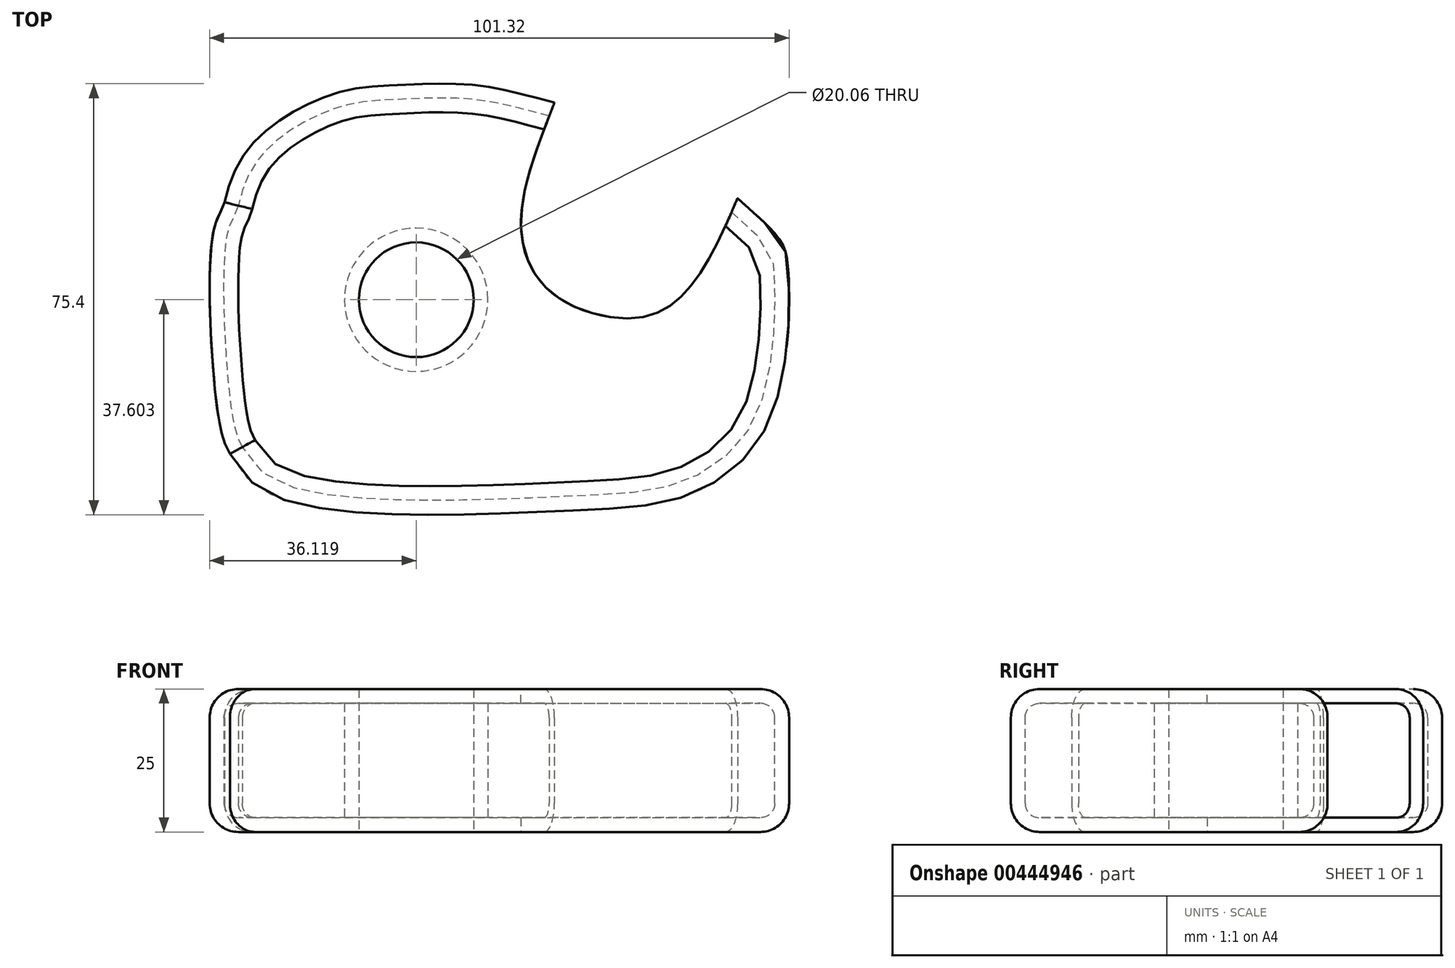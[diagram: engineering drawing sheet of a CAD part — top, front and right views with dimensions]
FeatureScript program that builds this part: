
annotation { "Feature Type Name" : "Feature", "Feature Type Description" : "" }
export const myFeature = defineFeature(function(context is Context, id is Id, definition is map)
    precondition{}
    {
        {
            var Q0;
            Q0=qCreatedBy(makeId("Top.planeOp"),FACE);
            var sketch = newSketch(context, id + "F0", { "sketchPlane" : qUnion([Q0])});
            skFitSpline(sketch, "E0", {"points": [v(10.23, 26.14) * mm, v(4.38, 5.02) * mm, v(10.12, -7.4) * mm, v(25.3, -11.43) * mm, v(34.2, -5.78) * mm, v(42.24, 9.43) * mm], "startDerivative": vector(-36.1, -93.3) * mm, "endDerivative": vector(37.02, 88.07) * mm});
            skFitSpline(sketch, "E1", {"points": [v(42.24, 9.43) * mm, v(49.55, 2.28) * mm, v(51.16, -4) * mm, v(47.56, -30.03) * mm, v(33.38, -42.58) * mm, v(16.53, -45.04) * mm, v(-28.97, -45.06) * mm, v(-46.53, -35.31) * mm], "startDerivative": vector(80.82, -73.63) * mm, "endDerivative": vector(-64.77, 129.9) * mm});
            skFitSpline(sketch, "E2", {"points": [v(10.23, 26.14) * mm, v(-3.65, 29.2) * mm, v(-17.94, 29.15) * mm, v(-27.99, 27.8) * mm, v(-41.27, 20.28) * mm, v(-47.46, 8.72) * mm], "startDerivative": vector(-70.66, 18.44) * mm, "endDerivative": vector(-15.22, -71.77) * mm});
            skFitSpline(sketch, "E3", {"points": [v(-47.46, 8.72) * mm, v(-49.26, 4.23) * mm, v(-49.26, -22.78) * mm, v(-46.53, -35.31) * mm], "startDerivative": vector(-5.49, -19.44) * mm, "endDerivative": vector(13.44, -22.4) * mm});
            skCircle(sketch, "E4", {"center": v(-13.94, -8.35) * mm, "radius": 10.03 * mm});
            skSolve(sketch);
        }
        {
            var Q0;
            Q0 = qSketchRegion(id + "F0", true);
            extrude(context, id + "F1", {"entities" : qUnion([Q0]), "depth" : 25 * mm});
        }
        {
            var Q0;
            Q0=makeQuery(id+"F1.opExtrude","CAP_EDGE",EDGE,{"disambiguationData":[OSD([sQuery(id+"F0.wireOp",EDGE,"E2")])],"isStart":false});
            var Q1;
            Q1=makeQuery(id+"F1.opExtrude","CAP_EDGE",EDGE,{"disambiguationData":[OSD([sQuery(id+"F0.wireOp",EDGE,"E3")])],"isStart":false});
            var Q2;
            Q2=makeQuery(id+"F1.opExtrude","CAP_EDGE",EDGE,{"disambiguationData":[OSD([sQuery(id+"F0.wireOp",EDGE,"E1")])],"isStart":false});
            fillet(context, id + "F2", {"entities" : qUnion([Q0, Q1, Q2]), "radius" : 5 * mm, "tangentPropagation" : true, "allowEdgeOverflow" : false});
        }
        {
            var Q0;
            Q0=makeQuery(id+"F1.opExtrude","CAP_EDGE",EDGE,{"disambiguationData":[OSD([sQuery(id+"F0.wireOp",EDGE,"E2")])],"isStart":true});
            var Q1;
            Q1=makeQuery(id+"F1.opExtrude","CAP_EDGE",EDGE,{"disambiguationData":[OSD([sQuery(id+"F0.wireOp",EDGE,"E1")])],"isStart":true});
            var Q2;
            Q2=makeQuery(id+"F1.opExtrude","CAP_EDGE",EDGE,{"disambiguationData":[OSD([sQuery(id+"F0.wireOp",EDGE,"E3")])],"isStart":true});
            fillet(context, id + "F3", {"entities" : qUnion([Q0, Q1, Q2]), "radius" : 5 * mm, "tangentPropagation" : true, "allowEdgeOverflow" : false});
        }
        {
            var Q0;
            Q0=makeQuery(id+"F1.opExtrude","SWEPT_FACE",FACE,{"disambiguationData":[OSD([sQuery(id+"F0.wireOp",EDGE,"E0")])]});
            shell(context, id + "F4", {"entities" : qUnion([Q0]), "thickness" : 2.5 * mm});
        }
    });
